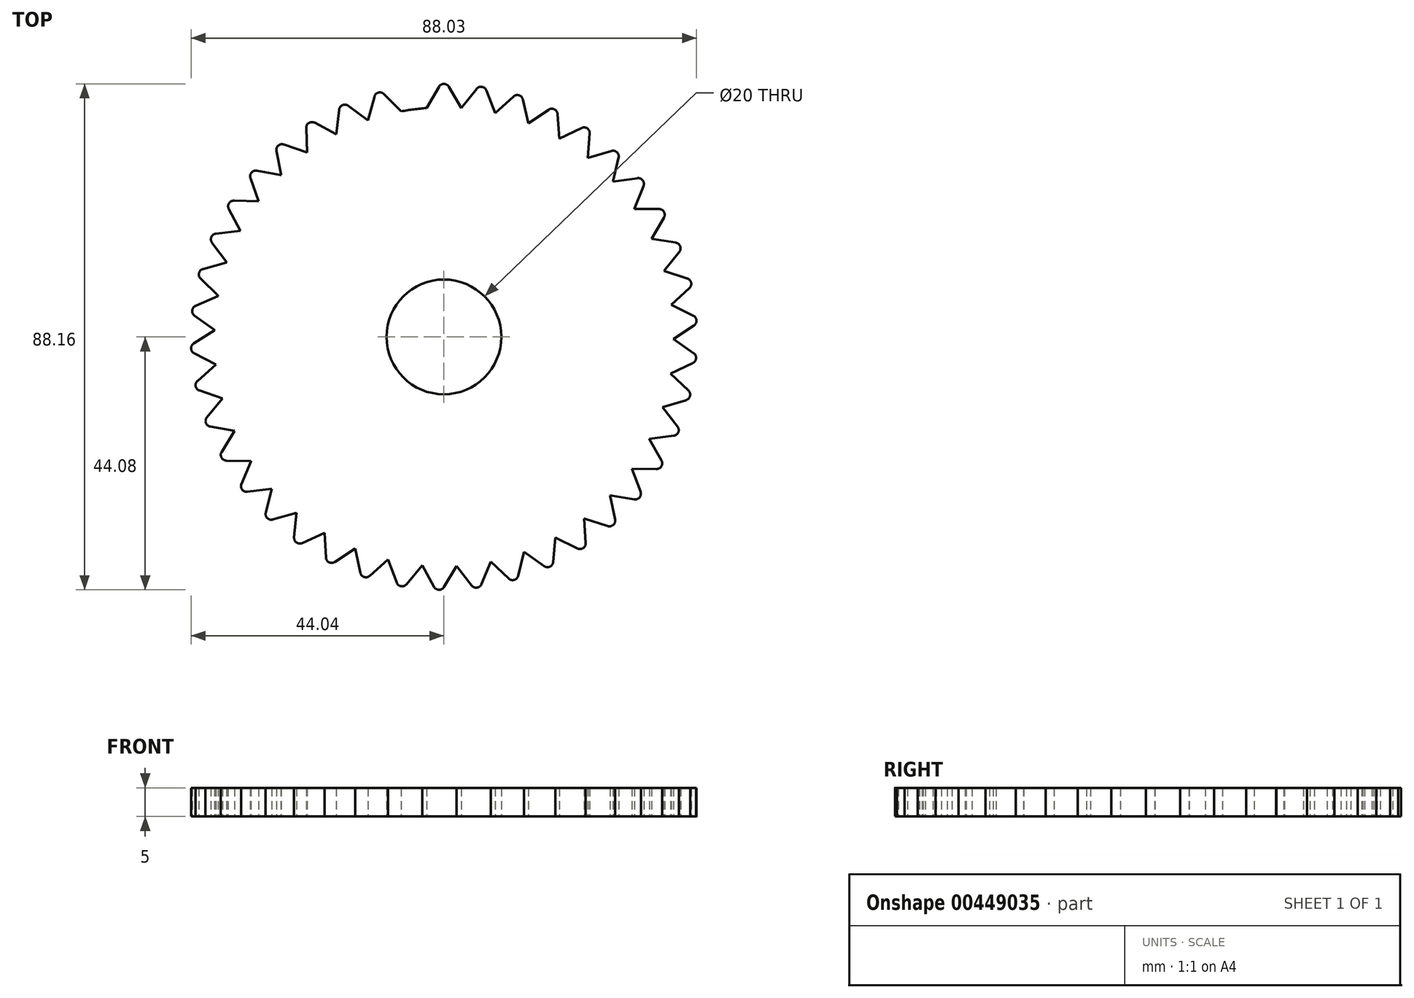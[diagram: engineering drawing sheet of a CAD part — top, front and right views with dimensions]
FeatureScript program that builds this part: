
annotation { "Feature Type Name" : "Feature", "Feature Type Description" : "" }
export const myFeature = defineFeature(function(context is Context, id is Id, definition is map)
    precondition{}
    {
        {
            var Q0;
            Q0=qCreatedBy(makeId("Top.planeOp"),FACE);
            var sketch = newSketch(context, id + "F0", { "sketchPlane" : qUnion([Q0])});
            skCircle(sketch, "E0", {"center": v(0, 0) * mm, "radius": 10 * mm});
            skArc(sketch, "E1.0", {"start": v(-3, 39.89) * mm, "mid": v(0, -40) * mm, "end": v(3, 39.89) * mm});
            skLineSegment(sketch, "E2", {"start": v(-3, 39.89) * mm, "end": v(-0.87, 43.58) * mm});
            skLineSegment(sketch, "E3", {"start": v(0.87, 43.58) * mm, "end": v(3, 39.89) * mm});
            skPoint(sketch, "E4.visualSharp", {"position": v(0, 45.08) * mm});
            skArc(sketch, "E4.filletArc", {"start": v(0.87, 43.58) * mm, "mid": v(0, 44.08) * mm, "end": v(-0.87, 43.58) * mm});
            skLineSegment(sketch, "E5.1.0", {"start": v(3.02, 39.89) * mm, "end": v(5.68, 43.22) * mm});
            skArc(sketch, "E5.1.1", {"start": v(7.4, 42.96) * mm, "mid": v(6.61, 43.58) * mm, "end": v(5.68, 43.22) * mm});
            skLineSegment(sketch, "E5.1.2", {"start": v(7.4, 42.96) * mm, "end": v(8.95, 38.99) * mm});
            skLineSegment(sketch, "E5.2.0", {"start": v(8.96, 38.98) * mm, "end": v(12.1, 41.88) * mm});
            skArc(sketch, "E5.2.1", {"start": v(13.75, 41.37) * mm, "mid": v(13.07, 42.1) * mm, "end": v(12.1, 41.88) * mm});
            skLineSegment(sketch, "E5.2.2", {"start": v(13.75, 41.37) * mm, "end": v(14.7, 37.2) * mm});
            skLineSegment(sketch, "E5.3.0", {"start": v(14.7, 37.2) * mm, "end": v(18.24, 39.6) * mm});
            skArc(sketch, "E5.3.1", {"start": v(19.8, 38.84) * mm, "mid": v(19.24, 39.66) * mm, "end": v(18.24, 39.6) * mm});
            skLineSegment(sketch, "E5.3.2", {"start": v(19.8, 38.84) * mm, "end": v(20.1, 34.58) * mm});
            skLineSegment(sketch, "E5.4.0", {"start": v(20.12, 34.57) * mm, "end": v(23.97, 36.4) * mm});
            skArc(sketch, "E5.4.1", {"start": v(25.4, 35.43) * mm, "mid": v(24.97, 36.33) * mm, "end": v(23.97, 36.4) * mm});
            skLineSegment(sketch, "E5.4.2", {"start": v(25.4, 35.43) * mm, "end": v(25.06, 31.17) * mm});
            skLineSegment(sketch, "E5.5.0", {"start": v(25.08, 31.16) * mm, "end": v(29.16, 32.4) * mm});
            skArc(sketch, "E5.5.1", {"start": v(30.43, 31.22) * mm, "mid": v(30.14, 32.17) * mm, "end": v(29.16, 32.4) * mm});
            skLineSegment(sketch, "E5.5.2", {"start": v(30.43, 31.22) * mm, "end": v(29.46, 27.06) * mm});
            skLineSegment(sketch, "E5.6.0", {"start": v(29.47, 27.05) * mm, "end": v(33.7, 27.66) * mm});
            skArc(sketch, "E5.6.1", {"start": v(34.76, 26.3) * mm, "mid": v(34.62, 27.3) * mm, "end": v(33.7, 27.66) * mm});
            skLineSegment(sketch, "E5.6.2", {"start": v(34.76, 26.3) * mm, "end": v(33.18, 22.34) * mm});
            skLineSegment(sketch, "E5.7.0", {"start": v(33.2, 22.32) * mm, "end": v(37.46, 22.3) * mm});
            skArc(sketch, "E5.7.1", {"start": v(38.31, 20.8) * mm, "mid": v(38.32, 21.8) * mm, "end": v(37.46, 22.3) * mm});
            skLineSegment(sketch, "E5.7.2", {"start": v(38.31, 20.8) * mm, "end": v(36.16, 17.1) * mm});
            skLineSegment(sketch, "E5.8.0", {"start": v(36.16, 17.1) * mm, "end": v(40.38, 16.43) * mm});
            skArc(sketch, "E5.8.1", {"start": v(41, 14.81) * mm, "mid": v(41.16, 15.8) * mm, "end": v(40.38, 16.43) * mm});
            skLineSegment(sketch, "E5.8.2", {"start": v(41, 14.81) * mm, "end": v(38.31, 11.5) * mm});
            skLineSegment(sketch, "E5.9.0", {"start": v(38.32, 11.48) * mm, "end": v(42.39, 10.19) * mm});
            skArc(sketch, "E5.9.1", {"start": v(42.76, 8.5) * mm, "mid": v(43.06, 9.45) * mm, "end": v(42.39, 10.19) * mm});
            skLineSegment(sketch, "E5.9.2", {"start": v(42.76, 8.5) * mm, "end": v(39.6, 5.62) * mm});
            skLineSegment(sketch, "E5.10.0", {"start": v(39.6, 5.6) * mm, "end": v(43.43, 3.71) * mm});
            skArc(sketch, "E5.10.1", {"start": v(43.55, 1.99) * mm, "mid": v(43.99, 2.88) * mm, "end": v(43.43, 3.71) * mm});
            skLineSegment(sketch, "E5.10.2", {"start": v(43.55, 1.99) * mm, "end": v(40, -0.38) * mm});
            skLineSegment(sketch, "E5.11.0", {"start": v(40, -0.4) * mm, "end": v(43.5, -2.84) * mm});
            skArc(sketch, "E5.11.1", {"start": v(43.35, -4.57) * mm, "mid": v(43.92, -3.75) * mm, "end": v(43.5, -2.84) * mm});
            skLineSegment(sketch, "E5.11.2", {"start": v(43.35, -4.57) * mm, "end": v(39.49, -6.38) * mm});
            skLineSegment(sketch, "E5.12.0", {"start": v(39.49, -6.4) * mm, "end": v(42.58, -9.33) * mm});
            skArc(sketch, "E5.12.1", {"start": v(42.18, -11.02) * mm, "mid": v(42.87, -10.3) * mm, "end": v(42.58, -9.33) * mm});
            skLineSegment(sketch, "E5.12.2", {"start": v(42.18, -11.02) * mm, "end": v(38.08, -12.23) * mm});
            skLineSegment(sketch, "E5.13.0", {"start": v(38.08, -12.24) * mm, "end": v(40.7, -15.61) * mm});
            skArc(sketch, "E5.13.1", {"start": v(40.05, -17.22) * mm, "mid": v(40.84, -16.6) * mm, "end": v(40.7, -15.61) * mm});
            skLineSegment(sketch, "E5.13.2", {"start": v(40.05, -17.22) * mm, "end": v(35.82, -17.8) * mm});
            skLineSegment(sketch, "E5.14.0", {"start": v(35.81, -17.82) * mm, "end": v(37.9, -21.54) * mm});
            skArc(sketch, "E5.14.1", {"start": v(37.01, -23.03) * mm, "mid": v(37.89, -22.54) * mm, "end": v(37.9, -21.54) * mm});
            skLineSegment(sketch, "E5.14.2", {"start": v(37.01, -23.03) * mm, "end": v(32.75, -22.97) * mm});
            skLineSegment(sketch, "E5.15.0", {"start": v(32.74, -22.99) * mm, "end": v(34.24, -26.98) * mm});
            skArc(sketch, "E5.15.1", {"start": v(33.14, -28.32) * mm, "mid": v(34.08, -27.97) * mm, "end": v(34.24, -26.98) * mm});
            skLineSegment(sketch, "E5.15.2", {"start": v(33.14, -28.32) * mm, "end": v(28.93, -27.62) * mm});
            skLineSegment(sketch, "E5.16.0", {"start": v(28.92, -27.63) * mm, "end": v(29.8, -31.8) * mm});
            skArc(sketch, "E5.16.1", {"start": v(28.52, -32.97) * mm, "mid": v(29.5, -32.76) * mm, "end": v(29.8, -31.8) * mm});
            skLineSegment(sketch, "E5.16.2", {"start": v(28.52, -32.97) * mm, "end": v(24.46, -31.65) * mm});
            skLineSegment(sketch, "E5.17.0", {"start": v(24.45, -31.66) * mm, "end": v(24.7, -35.92) * mm});
            skArc(sketch, "E5.17.1", {"start": v(23.25, -36.87) * mm, "mid": v(24.25, -36.81) * mm, "end": v(24.7, -35.92) * mm});
            skLineSegment(sketch, "E5.17.2", {"start": v(23.25, -36.87) * mm, "end": v(19.44, -34.96) * mm});
            skLineSegment(sketch, "E5.18.0", {"start": v(19.42, -34.97) * mm, "end": v(19.03, -39.22) * mm});
            skArc(sketch, "E5.18.1", {"start": v(17.46, -39.94) * mm, "mid": v(18.46, -40.03) * mm, "end": v(19.03, -39.22) * mm});
            skLineSegment(sketch, "E5.18.2", {"start": v(17.46, -39.94) * mm, "end": v(13.97, -37.48) * mm});
            skLineSegment(sketch, "E5.19.0", {"start": v(13.96, -37.48) * mm, "end": v(12.94, -41.63) * mm});
            skArc(sketch, "E5.19.1", {"start": v(11.27, -42.1) * mm, "mid": v(12.24, -42.35) * mm, "end": v(12.94, -41.63) * mm});
            skLineSegment(sketch, "E5.19.2", {"start": v(11.27, -42.1) * mm, "end": v(8.2, -39.15) * mm});
            skLineSegment(sketch, "E5.20.0", {"start": v(8.18, -39.15) * mm, "end": v(6.55, -43.1) * mm});
            skArc(sketch, "E5.20.1", {"start": v(4.83, -43.32) * mm, "mid": v(5.75, -43.7) * mm, "end": v(6.55, -43.1) * mm});
            skLineSegment(sketch, "E5.20.2", {"start": v(4.83, -43.32) * mm, "end": v(2.23, -39.94) * mm});
            skLineSegment(sketch, "E5.21.0", {"start": v(2.22, -39.94) * mm, "end": v(0.01, -43.6) * mm});
            skArc(sketch, "E5.21.1", {"start": v(-1.72, -43.56) * mm, "mid": v(-0.87, -44.07) * mm, "end": v(0.01, -43.6) * mm});
            skLineSegment(sketch, "E5.21.2", {"start": v(-1.72, -43.56) * mm, "end": v(-3.78, -39.82) * mm});
            skLineSegment(sketch, "E5.22.0", {"start": v(-3.8, -39.82) * mm, "end": v(-6.53, -43.1) * mm});
            skArc(sketch, "E5.22.1", {"start": v(-8.23, -42.8) * mm, "mid": v(-7.47, -43.45) * mm, "end": v(-6.53, -43.1) * mm});
            skLineSegment(sketch, "E5.22.2", {"start": v(-8.23, -42.8) * mm, "end": v(-9.71, -38.8) * mm});
            skLineSegment(sketch, "E5.23.0", {"start": v(-9.73, -38.8) * mm, "end": v(-12.92, -41.63) * mm});
            skArc(sketch, "E5.23.1", {"start": v(-14.56, -41.09) * mm, "mid": v(-13.9, -41.84) * mm, "end": v(-12.92, -41.63) * mm});
            skLineSegment(sketch, "E5.23.2", {"start": v(-14.56, -41.09) * mm, "end": v(-15.42, -36.9) * mm});
            skLineSegment(sketch, "E5.24.0", {"start": v(-15.44, -36.9) * mm, "end": v(-19.01, -39.23) * mm});
            skArc(sketch, "E5.24.1", {"start": v(-20.56, -38.44) * mm, "mid": v(-20.01, -39.28) * mm, "end": v(-19.01, -39.23) * mm});
            skLineSegment(sketch, "E5.24.2", {"start": v(-20.56, -38.44) * mm, "end": v(-20.78, -34.18) * mm});
            skLineSegment(sketch, "E5.25.0", {"start": v(-20.8, -34.17) * mm, "end": v(-24.68, -35.93) * mm});
            skArc(sketch, "E5.25.1", {"start": v(-26.1, -34.92) * mm, "mid": v(-25.68, -35.83) * mm, "end": v(-24.68, -35.93) * mm});
            skLineSegment(sketch, "E5.25.2", {"start": v(-26.1, -34.92) * mm, "end": v(-25.67, -30.67) * mm});
            skLineSegment(sketch, "E5.26.0", {"start": v(-25.68, -30.66) * mm, "end": v(-29.8, -31.82) * mm});
            skArc(sketch, "E5.26.1", {"start": v(-31.03, -30.61) * mm, "mid": v(-30.76, -31.58) * mm, "end": v(-29.8, -31.82) * mm});
            skLineSegment(sketch, "E5.26.2", {"start": v(-31.03, -30.61) * mm, "end": v(-29.98, -26.48) * mm});
            skLineSegment(sketch, "E5.27.0", {"start": v(-30, -26.47) * mm, "end": v(-34.23, -27) * mm});
            skArc(sketch, "E5.27.1", {"start": v(-35.27, -25.61) * mm, "mid": v(-35.15, -26.6) * mm, "end": v(-34.23, -27) * mm});
            skLineSegment(sketch, "E5.27.2", {"start": v(-35.27, -25.61) * mm, "end": v(-33.61, -21.68) * mm});
            skLineSegment(sketch, "E5.28.0", {"start": v(-33.62, -21.67) * mm, "end": v(-37.89, -21.56) * mm});
            skArc(sketch, "E5.28.1", {"start": v(-38.72, -20.04) * mm, "mid": v(-38.74, -21.03) * mm, "end": v(-37.89, -21.56) * mm});
            skLineSegment(sketch, "E5.28.2", {"start": v(-38.72, -20.04) * mm, "end": v(-36.49, -16.4) * mm});
            skLineSegment(sketch, "E5.29.0", {"start": v(-36.5, -16.38) * mm, "end": v(-40.7, -15.63) * mm});
            skArc(sketch, "E5.29.1", {"start": v(-41.28, -14) * mm, "mid": v(-41.46, -14.99) * mm, "end": v(-40.7, -15.63) * mm});
            skLineSegment(sketch, "E5.29.2", {"start": v(-41.28, -14) * mm, "end": v(-38.53, -10.74) * mm});
            skLineSegment(sketch, "E5.30.0", {"start": v(-38.54, -10.72) * mm, "end": v(-42.58, -9.35) * mm});
            skArc(sketch, "E5.30.1", {"start": v(-42.92, -7.65) * mm, "mid": v(-43.24, -8.6) * mm, "end": v(-42.58, -9.35) * mm});
            skLineSegment(sketch, "E5.30.2", {"start": v(-42.92, -7.65) * mm, "end": v(-39.7, -4.84) * mm});
            skLineSegment(sketch, "E5.31.0", {"start": v(-39.7, -4.82) * mm, "end": v(-43.5, -2.86) * mm});
            skArc(sketch, "E5.31.1", {"start": v(-43.58, -1.13) * mm, "mid": v(-44.04, -2.02) * mm, "end": v(-43.5, -2.86) * mm});
            skLineSegment(sketch, "E5.31.2", {"start": v(-43.58, -1.13) * mm, "end": v(-39.98, 1.17) * mm});
            skLineSegment(sketch, "E5.32.0", {"start": v(-39.98, 1.19) * mm, "end": v(-43.44, 3.7) * mm});
            skArc(sketch, "E5.32.1", {"start": v(-43.25, 5.42) * mm, "mid": v(-43.84, 4.6) * mm, "end": v(-43.44, 3.7) * mm});
            skLineSegment(sketch, "E5.32.2", {"start": v(-43.25, 5.42) * mm, "end": v(-39.36, 7.15) * mm});
            skLineSegment(sketch, "E5.33.0", {"start": v(-39.35, 7.17) * mm, "end": v(-42.4, 10.17) * mm});
            skArc(sketch, "E5.33.1", {"start": v(-41.95, 11.84) * mm, "mid": v(-42.66, 11.13) * mm, "end": v(-42.4, 10.17) * mm});
            skLineSegment(sketch, "E5.33.2", {"start": v(-41.95, 11.84) * mm, "end": v(-37.84, 12.97) * mm});
            skLineSegment(sketch, "E5.34.0", {"start": v(-37.83, 12.99) * mm, "end": v(-40.39, 16.4) * mm});
            skArc(sketch, "E5.34.1", {"start": v(-39.7, 18) * mm, "mid": v(-40.5, 17.4) * mm, "end": v(-40.39, 16.4) * mm});
            skLineSegment(sketch, "E5.34.2", {"start": v(-39.7, 18) * mm, "end": v(-35.46, 18.5) * mm});
            skLineSegment(sketch, "E5.35.0", {"start": v(-35.46, 18.52) * mm, "end": v(-37.47, 22.28) * mm});
            skArc(sketch, "E5.35.1", {"start": v(-36.55, 23.75) * mm, "mid": v(-37.44, 23.28) * mm, "end": v(-37.47, 22.28) * mm});
            skLineSegment(sketch, "E5.35.2", {"start": v(-36.55, 23.75) * mm, "end": v(-32.29, 23.61) * mm});
            skLineSegment(sketch, "E5.36.0", {"start": v(-32.28, 23.62) * mm, "end": v(-33.7, 27.65) * mm});
            skArc(sketch, "E5.36.1", {"start": v(-32.58, 28.96) * mm, "mid": v(-33.52, 28.63) * mm, "end": v(-33.7, 27.65) * mm});
            skLineSegment(sketch, "E5.36.2", {"start": v(-32.58, 28.96) * mm, "end": v(-28.38, 28.19) * mm});
            skLineSegment(sketch, "E5.37.0", {"start": v(-28.37, 28.2) * mm, "end": v(-29.18, 32.39) * mm});
            skArc(sketch, "E5.37.1", {"start": v(-27.87, 33.52) * mm, "mid": v(-28.85, 33.33) * mm, "end": v(-29.18, 32.39) * mm});
            skLineSegment(sketch, "E5.37.2", {"start": v(-27.87, 33.52) * mm, "end": v(-23.83, 32.12) * mm});
            skLineSegment(sketch, "E5.38.0", {"start": v(-23.82, 32.13) * mm, "end": v(-23.99, 36.4) * mm});
            skArc(sketch, "E5.38.1", {"start": v(-22.52, 37.32) * mm, "mid": v(-23.52, 37.28) * mm, "end": v(-23.99, 36.4) * mm});
            skLineSegment(sketch, "E5.38.2", {"start": v(-22.52, 37.32) * mm, "end": v(-18.75, 35.33) * mm});
            skLineSegment(sketch, "E5.39.0", {"start": v(-18.73, 35.34) * mm, "end": v(-18.26, 39.58) * mm});
            skArc(sketch, "E5.39.1", {"start": v(-16.67, 40.28) * mm, "mid": v(-17.67, 40.39) * mm, "end": v(-18.26, 39.58) * mm});
            skLineSegment(sketch, "E5.39.2", {"start": v(-16.67, 40.28) * mm, "end": v(-13.24, 37.75) * mm});
            skLineSegment(sketch, "E5.anchor1", {"start": v(0, 0) * mm, "end": v(-3, 39.89) * mm, "construction": true});
            skLineSegment(sketch, "E5.anchor2", {"start": v(0, 0) * mm, "end": v(-13.22, 37.75) * mm, "construction": true});
            skLineSegment(sketch, "E6.1.40.0", {"start": v(-13.22, 37.75) * mm, "end": v(-12.12, 41.87) * mm});
            skArc(sketch, "E6.3.40.0", {"start": v(-10.44, 42.32) * mm, "mid": v(-11.4, 42.58) * mm, "end": v(-12.12, 41.87) * mm});
            skLineSegment(sketch, "E6.7.40.0", {"start": v(-10.44, 42.32) * mm, "end": v(-7.43, 39.3) * mm});
            skSolve(sketch);
        }
        {
            var Q0;
            {var subQ0=sQuery(id+"F0.wireOp",EDGE,"E5.1.0");Q0=makeQuery(id+"F0.imprint","IMPRINT",FACE,{"disambiguationData":[TD([[makeQuery(id+"F0.imprint","IMPRINT",EDGE,{"derivedFrom":subQ0}),-1.0]])]});}
            var Q1;
            {var subQ0=sQuery(id+"F0.wireOp",EDGE,"E5.2.0");Q1=makeQuery(id+"F0.imprint","IMPRINT",FACE,{"disambiguationData":[TD([[makeQuery(id+"F0.imprint","IMPRINT",EDGE,{"derivedFrom":subQ0}),-1.0]])]});}
            var Q2;
            {var subQ0=sQuery(id+"F0.wireOp",EDGE,"E5.3.0");Q2=makeQuery(id+"F0.imprint","IMPRINT",FACE,{"disambiguationData":[TD([[makeQuery(id+"F0.imprint","IMPRINT",EDGE,{"derivedFrom":subQ0}),-1.0]])]});}
            var Q3;
            {var subQ0=sQuery(id+"F0.wireOp",EDGE,"E5.5.0");Q3=makeQuery(id+"F0.imprint","IMPRINT",FACE,{"disambiguationData":[TD([[makeQuery(id+"F0.imprint","IMPRINT",EDGE,{"derivedFrom":subQ0}),-1.0]])]});}
            var Q4;
            {var subQ0=sQuery(id+"F0.wireOp",EDGE,"E5.6.0");Q4=makeQuery(id+"F0.imprint","IMPRINT",FACE,{"disambiguationData":[TD([[makeQuery(id+"F0.imprint","IMPRINT",EDGE,{"derivedFrom":subQ0}),-1.0]])]});}
            var Q5;
            {var subQ0=sQuery(id+"F0.wireOp",EDGE,"E5.8.0");Q5=makeQuery(id+"F0.imprint","IMPRINT",FACE,{"disambiguationData":[TD([[makeQuery(id+"F0.imprint","IMPRINT",EDGE,{"derivedFrom":subQ0}),-1.0]])]});}
            var Q6;
            {var subQ0=sQuery(id+"F0.wireOp",EDGE,"E5.4.0");Q6=makeQuery(id+"F0.imprint","IMPRINT",FACE,{"disambiguationData":[TD([[makeQuery(id+"F0.imprint","IMPRINT",EDGE,{"derivedFrom":subQ0}),-1.0]])]});}
            var Q7;
            {var subQ0=sQuery(id+"F0.wireOp",EDGE,"E5.7.0");Q7=makeQuery(id+"F0.imprint","IMPRINT",FACE,{"disambiguationData":[TD([[makeQuery(id+"F0.imprint","IMPRINT",EDGE,{"derivedFrom":subQ0}),-1.0]])]});}
            var Q8;
            {var subQ0=sQuery(id+"F0.wireOp",EDGE,"E5.9.0");Q8=makeQuery(id+"F0.imprint","IMPRINT",FACE,{"disambiguationData":[TD([[makeQuery(id+"F0.imprint","IMPRINT",EDGE,{"derivedFrom":subQ0}),-1.0]])]});}
            var Q9;
            {var subQ0=sQuery(id+"F0.wireOp",EDGE,"E5.10.0");Q9=makeQuery(id+"F0.imprint","IMPRINT",FACE,{"disambiguationData":[TD([[makeQuery(id+"F0.imprint","IMPRINT",EDGE,{"derivedFrom":subQ0}),-1.0]])]});}
            var Q10;
            {var subQ0=sQuery(id+"F0.wireOp",EDGE,"E5.11.0");Q10=makeQuery(id+"F0.imprint","IMPRINT",FACE,{"disambiguationData":[TD([[makeQuery(id+"F0.imprint","IMPRINT",EDGE,{"derivedFrom":subQ0}),-1.0]])]});}
            var Q11;
            {var subQ0=sQuery(id+"F0.wireOp",EDGE,"E5.12.0");Q11=makeQuery(id+"F0.imprint","IMPRINT",FACE,{"disambiguationData":[TD([[makeQuery(id+"F0.imprint","IMPRINT",EDGE,{"derivedFrom":subQ0}),-1.0]])]});}
            var Q12;
            {var subQ0=sQuery(id+"F0.wireOp",EDGE,"E5.13.0");Q12=makeQuery(id+"F0.imprint","IMPRINT",FACE,{"disambiguationData":[TD([[makeQuery(id+"F0.imprint","IMPRINT",EDGE,{"derivedFrom":subQ0}),-1.0]])]});}
            var Q13;
            {var subQ0=sQuery(id+"F0.wireOp",EDGE,"E5.14.0");Q13=makeQuery(id+"F0.imprint","IMPRINT",FACE,{"disambiguationData":[TD([[makeQuery(id+"F0.imprint","IMPRINT",EDGE,{"derivedFrom":subQ0}),-1.0]])]});}
            var Q14;
            {var subQ0=sQuery(id+"F0.wireOp",EDGE,"E5.15.0");Q14=makeQuery(id+"F0.imprint","IMPRINT",FACE,{"disambiguationData":[TD([[makeQuery(id+"F0.imprint","IMPRINT",EDGE,{"derivedFrom":subQ0}),-1.0]])]});}
            var Q15;
            {var subQ0=sQuery(id+"F0.wireOp",EDGE,"E5.16.0");Q15=makeQuery(id+"F0.imprint","IMPRINT",FACE,{"disambiguationData":[TD([[makeQuery(id+"F0.imprint","IMPRINT",EDGE,{"derivedFrom":subQ0}),-1.0]])]});}
            var Q16;
            {var subQ0=sQuery(id+"F0.wireOp",EDGE,"E5.17.0");Q16=makeQuery(id+"F0.imprint","IMPRINT",FACE,{"disambiguationData":[TD([[makeQuery(id+"F0.imprint","IMPRINT",EDGE,{"derivedFrom":subQ0}),-1.0]])]});}
            var Q17;
            {var subQ0=sQuery(id+"F0.wireOp",EDGE,"E5.18.0");Q17=makeQuery(id+"F0.imprint","IMPRINT",FACE,{"disambiguationData":[TD([[makeQuery(id+"F0.imprint","IMPRINT",EDGE,{"derivedFrom":subQ0}),-1.0]])]});}
            var Q18;
            {var subQ0=sQuery(id+"F0.wireOp",EDGE,"E5.19.0");Q18=makeQuery(id+"F0.imprint","IMPRINT",FACE,{"disambiguationData":[TD([[makeQuery(id+"F0.imprint","IMPRINT",EDGE,{"derivedFrom":subQ0}),-1.0]])]});}
            var Q19;
            {var subQ0=sQuery(id+"F0.wireOp",EDGE,"E5.20.0");Q19=makeQuery(id+"F0.imprint","IMPRINT",FACE,{"disambiguationData":[TD([[makeQuery(id+"F0.imprint","IMPRINT",EDGE,{"derivedFrom":subQ0}),-1.0]])]});}
            var Q20;
            {var subQ0=sQuery(id+"F0.wireOp",EDGE,"E5.21.0");Q20=makeQuery(id+"F0.imprint","IMPRINT",FACE,{"disambiguationData":[TD([[makeQuery(id+"F0.imprint","IMPRINT",EDGE,{"derivedFrom":subQ0}),-1.0]])]});}
            var Q21;
            {var subQ0=sQuery(id+"F0.wireOp",EDGE,"E5.22.0");Q21=makeQuery(id+"F0.imprint","IMPRINT",FACE,{"disambiguationData":[TD([[makeQuery(id+"F0.imprint","IMPRINT",EDGE,{"derivedFrom":subQ0}),-1.0]])]});}
            var Q22;
            {var subQ0=sQuery(id+"F0.wireOp",EDGE,"E5.23.0");Q22=makeQuery(id+"F0.imprint","IMPRINT",FACE,{"disambiguationData":[TD([[makeQuery(id+"F0.imprint","IMPRINT",EDGE,{"derivedFrom":subQ0}),-1.0]])]});}
            var Q23;
            {var subQ0=sQuery(id+"F0.wireOp",EDGE,"E5.24.0");Q23=makeQuery(id+"F0.imprint","IMPRINT",FACE,{"disambiguationData":[TD([[makeQuery(id+"F0.imprint","IMPRINT",EDGE,{"derivedFrom":subQ0}),-1.0]])]});}
            var Q24;
            {var subQ0=sQuery(id+"F0.wireOp",EDGE,"E5.25.0");Q24=makeQuery(id+"F0.imprint","IMPRINT",FACE,{"disambiguationData":[TD([[makeQuery(id+"F0.imprint","IMPRINT",EDGE,{"derivedFrom":subQ0}),-1.0]])]});}
            var Q25;
            {var subQ0=sQuery(id+"F0.wireOp",EDGE,"E5.26.0");Q25=makeQuery(id+"F0.imprint","IMPRINT",FACE,{"disambiguationData":[TD([[makeQuery(id+"F0.imprint","IMPRINT",EDGE,{"derivedFrom":subQ0}),-1.0]])]});}
            var Q26;
            {var subQ0=sQuery(id+"F0.wireOp",EDGE,"E5.27.0");Q26=makeQuery(id+"F0.imprint","IMPRINT",FACE,{"disambiguationData":[TD([[makeQuery(id+"F0.imprint","IMPRINT",EDGE,{"derivedFrom":subQ0}),-1.0]])]});}
            var Q27;
            {var subQ0=sQuery(id+"F0.wireOp",EDGE,"E5.28.0");Q27=makeQuery(id+"F0.imprint","IMPRINT",FACE,{"disambiguationData":[TD([[makeQuery(id+"F0.imprint","IMPRINT",EDGE,{"derivedFrom":subQ0}),-1.0]])]});}
            var Q28;
            {var subQ0=sQuery(id+"F0.wireOp",EDGE,"E5.29.0");Q28=makeQuery(id+"F0.imprint","IMPRINT",FACE,{"disambiguationData":[TD([[makeQuery(id+"F0.imprint","IMPRINT",EDGE,{"derivedFrom":subQ0}),-1.0]])]});}
            var Q29;
            {var subQ0=sQuery(id+"F0.wireOp",EDGE,"E5.30.0");Q29=makeQuery(id+"F0.imprint","IMPRINT",FACE,{"disambiguationData":[TD([[makeQuery(id+"F0.imprint","IMPRINT",EDGE,{"derivedFrom":subQ0}),-1.0]])]});}
            var Q30;
            {var subQ0=sQuery(id+"F0.wireOp",EDGE,"E5.31.0");Q30=makeQuery(id+"F0.imprint","IMPRINT",FACE,{"disambiguationData":[TD([[makeQuery(id+"F0.imprint","IMPRINT",EDGE,{"derivedFrom":subQ0}),-1.0]])]});}
            var Q31;
            {var subQ0=sQuery(id+"F0.wireOp",EDGE,"E5.32.0");Q31=makeQuery(id+"F0.imprint","IMPRINT",FACE,{"disambiguationData":[TD([[makeQuery(id+"F0.imprint","IMPRINT",EDGE,{"derivedFrom":subQ0}),-1.0]])]});}
            var Q32;
            {var subQ0=sQuery(id+"F0.wireOp",EDGE,"E5.34.0");Q32=makeQuery(id+"F0.imprint","IMPRINT",FACE,{"disambiguationData":[TD([[makeQuery(id+"F0.imprint","IMPRINT",EDGE,{"derivedFrom":subQ0}),-1.0]])]});}
            var Q33;
            Q33=makeQuery(id+"F0.imprint","IMPRINT",FACE,{"disambiguationData":[TD([[makeQuery(id+"F0.imprint","IMPRINT",EDGE,{"derivedFrom":sQuery(id+"F0.wireOp",EDGE,"E0")}),-1.0]])]});
            var Q34;
            {var subQ0=sQuery(id+"F0.wireOp",EDGE,"E5.35.0");Q34=makeQuery(id+"F0.imprint","IMPRINT",FACE,{"disambiguationData":[TD([[makeQuery(id+"F0.imprint","IMPRINT",EDGE,{"derivedFrom":subQ0}),-1.0]])]});}
            var Q35;
            {var subQ0=sQuery(id+"F0.wireOp",EDGE,"E5.33.0");Q35=makeQuery(id+"F0.imprint","IMPRINT",FACE,{"disambiguationData":[TD([[makeQuery(id+"F0.imprint","IMPRINT",EDGE,{"derivedFrom":subQ0}),-1.0]])]});}
            var Q36;
            {var subQ0=sQuery(id+"F0.wireOp",EDGE,"E5.36.0");Q36=makeQuery(id+"F0.imprint","IMPRINT",FACE,{"disambiguationData":[TD([[makeQuery(id+"F0.imprint","IMPRINT",EDGE,{"derivedFrom":subQ0}),-1.0]])]});}
            var Q37;
            {var subQ0=sQuery(id+"F0.wireOp",EDGE,"E5.37.0");Q37=makeQuery(id+"F0.imprint","IMPRINT",FACE,{"disambiguationData":[TD([[makeQuery(id+"F0.imprint","IMPRINT",EDGE,{"derivedFrom":subQ0}),-1.0]])]});}
            var Q38;
            {var subQ0=sQuery(id+"F0.wireOp",EDGE,"E5.38.0");Q38=makeQuery(id+"F0.imprint","IMPRINT",FACE,{"disambiguationData":[TD([[makeQuery(id+"F0.imprint","IMPRINT",EDGE,{"derivedFrom":subQ0}),-1.0]])]});}
            var Q39;
            {var subQ0=sQuery(id+"F0.wireOp",EDGE,"E5.39.0");Q39=makeQuery(id+"F0.imprint","IMPRINT",FACE,{"disambiguationData":[TD([[makeQuery(id+"F0.imprint","IMPRINT",EDGE,{"derivedFrom":subQ0}),-1.0]])]});}
            var Q40;
            {var subQ0=sQuery(id+"F0.wireOp",EDGE,"E6.1.40.0");Q40=makeQuery(id+"F0.imprint","IMPRINT",FACE,{"disambiguationData":[TD([[makeQuery(id+"F0.imprint","IMPRINT",EDGE,{"derivedFrom":subQ0}),-1.0]])]});}
            extrude(context, id + "F1", {"entities" : qUnion([Q0, Q1, Q2, Q3, Q4, Q5, Q6, Q7, Q8, Q9, Q10, Q11, Q12, Q13, Q14, Q15, Q16, Q17, Q18, Q19, Q20, Q21, Q22, Q23, Q24, Q25, Q26, Q27, Q28, Q29, Q30, Q31, Q32, Q33, Q34, Q35, Q36, Q37, Q38, Q39, Q40]), "endBound" : BoundingType.SYMMETRIC, "depth" : 5 * mm});
        }
    });
